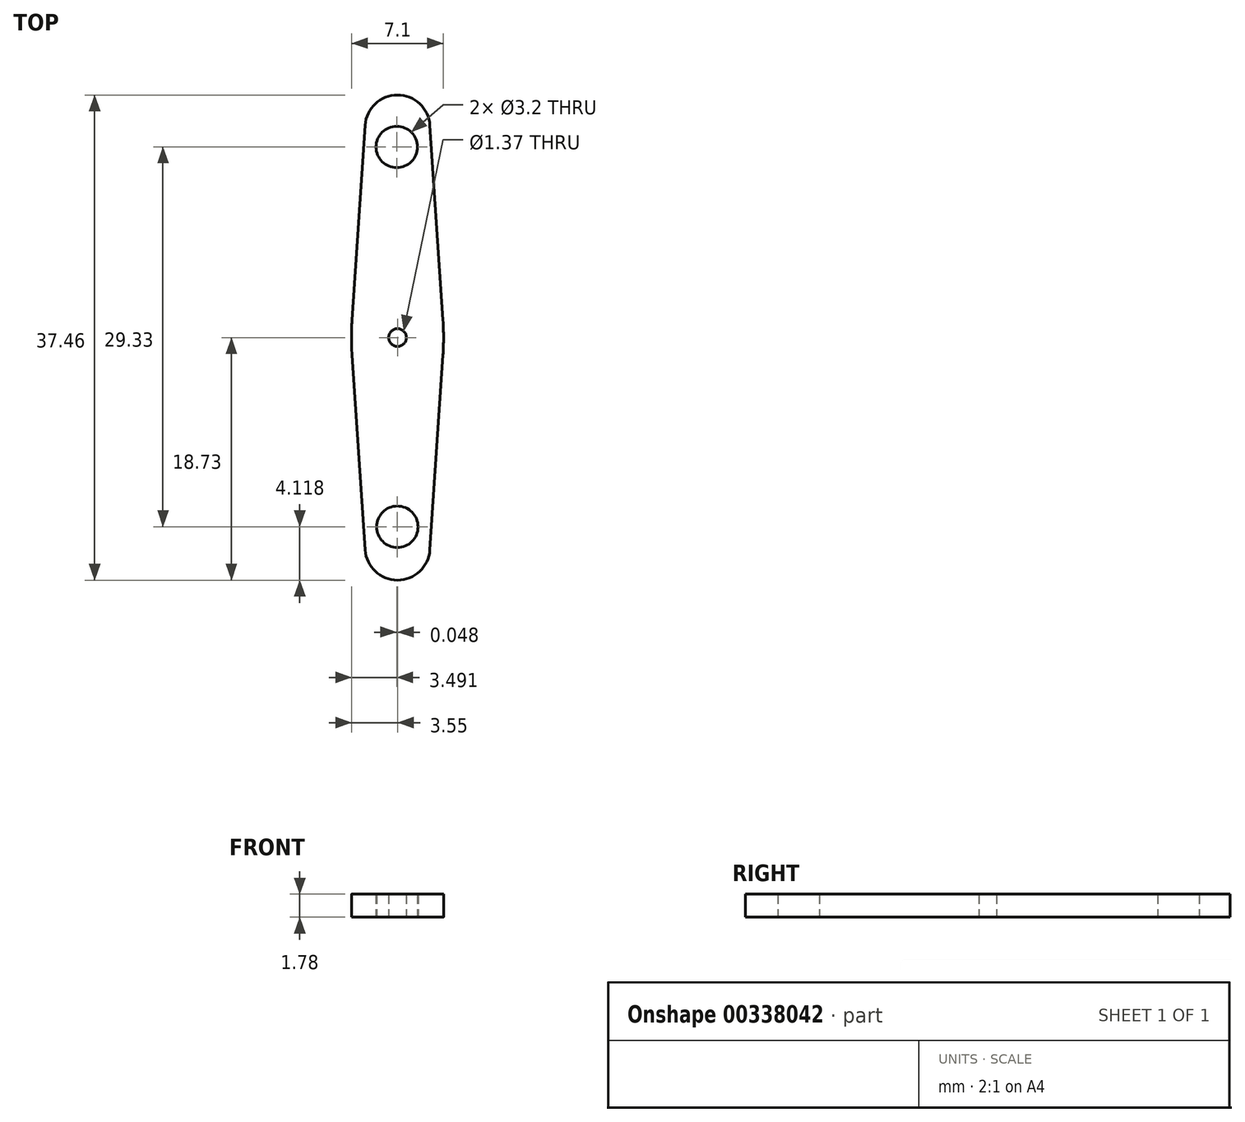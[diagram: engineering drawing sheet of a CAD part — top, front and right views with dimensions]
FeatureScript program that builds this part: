
annotation { "Feature Type Name" : "Feature", "Feature Type Description" : "" }
export const myFeature = defineFeature(function(context is Context, id is Id, definition is map)
    precondition{}
    {
        {
            var Q0;
            Q0=qCreatedBy(makeId("Top.planeOp"),FACE);
            var sketch = newSketch(context, id + "F0", { "sketchPlane" : qUnion([Q0])});
            skArc(sketch, "E0", {"start": v(2.5, 16.4) * mm, "mid": v(0, 18.73) * mm, "end": v(-2.5, 16.4) * mm});
            skPoint(sketch, "E1", {"position": v(0, 18.73) * mm});
            skLineSegment(sketch, "E2", {"start": v(-3.6, 0) * mm, "end": v(-2.5, 16.4) * mm});
            skLineSegment(sketch, "E3", {"start": v(3.6, 0) * mm, "end": v(2.5, 16.4) * mm});
            skCircle(sketch, "E4.0.2.0", {"center": v(-0.06, 14.72) * mm, "radius": 1.6 * mm});
            skPoint(sketch, "E5", {"position": v(0, 0) * mm});
            skLineSegment(sketch, "E6", {"start": v(-18.31, 0) * mm, "end": v(19.73, 0) * mm, "construction": true});
            skPoint(sketch, "E7.MirrorP", {"position": v(0, -18.73) * mm});
            skLineSegment(sketch, "E8.MirrorCS", {"start": v(-3.6, 0) * mm, "end": v(-2.5, -16.4) * mm});
            skArc(sketch, "E9.MirrorCS", {"start": v(2.5, -16.4) * mm, "mid": v(0, -18.73) * mm, "end": v(-2.5, -16.4) * mm});
            skLineSegment(sketch, "E10.MirrorCS", {"start": v(3.6, 0) * mm, "end": v(2.5, -16.4) * mm});
            skCircle(sketch, "E11", {"center": v(0, 0) * mm, "radius": 0.69 * mm});
            skCircle(sketch, "E12.MirrorC", {"center": v(-0.01, -14.61) * mm, "radius": 1.6 * mm});
            skSolve(sketch);
        }
        {
            var Q0;
            Q0=qSketchRegion(id+"F0",true);
            extrude(context, id + "F1", {"entities" : qUnion([Q0]), "depth" : 1.78 * mm});
        }
        {
            var Q0;
            Q0=makeQuery(id+"F1.opExtrude","SWEPT_EDGE",EDGE,{"disambiguationData":[OSD([sQuery(id+"F0.wireOp",EDGE,"E3"),sQuery(id+"F0.wireOp",EDGE,"E10.MirrorCS")])]});
            var Q1;
            Q1=makeQuery(id+"F1.opExtrude","SWEPT_EDGE",EDGE,{"disambiguationData":[OSD([sQuery(id+"F0.wireOp",EDGE,"E2"),sQuery(id+"F0.wireOp",EDGE,"E8.MirrorCS")])]});
            fillet(context, id + "F2", {"entities" : qUnion([Q0, Q1]), "radius" : 20 * mm, "tangentPropagation" : true, "allowEdgeOverflow" : false});
        }
    });
